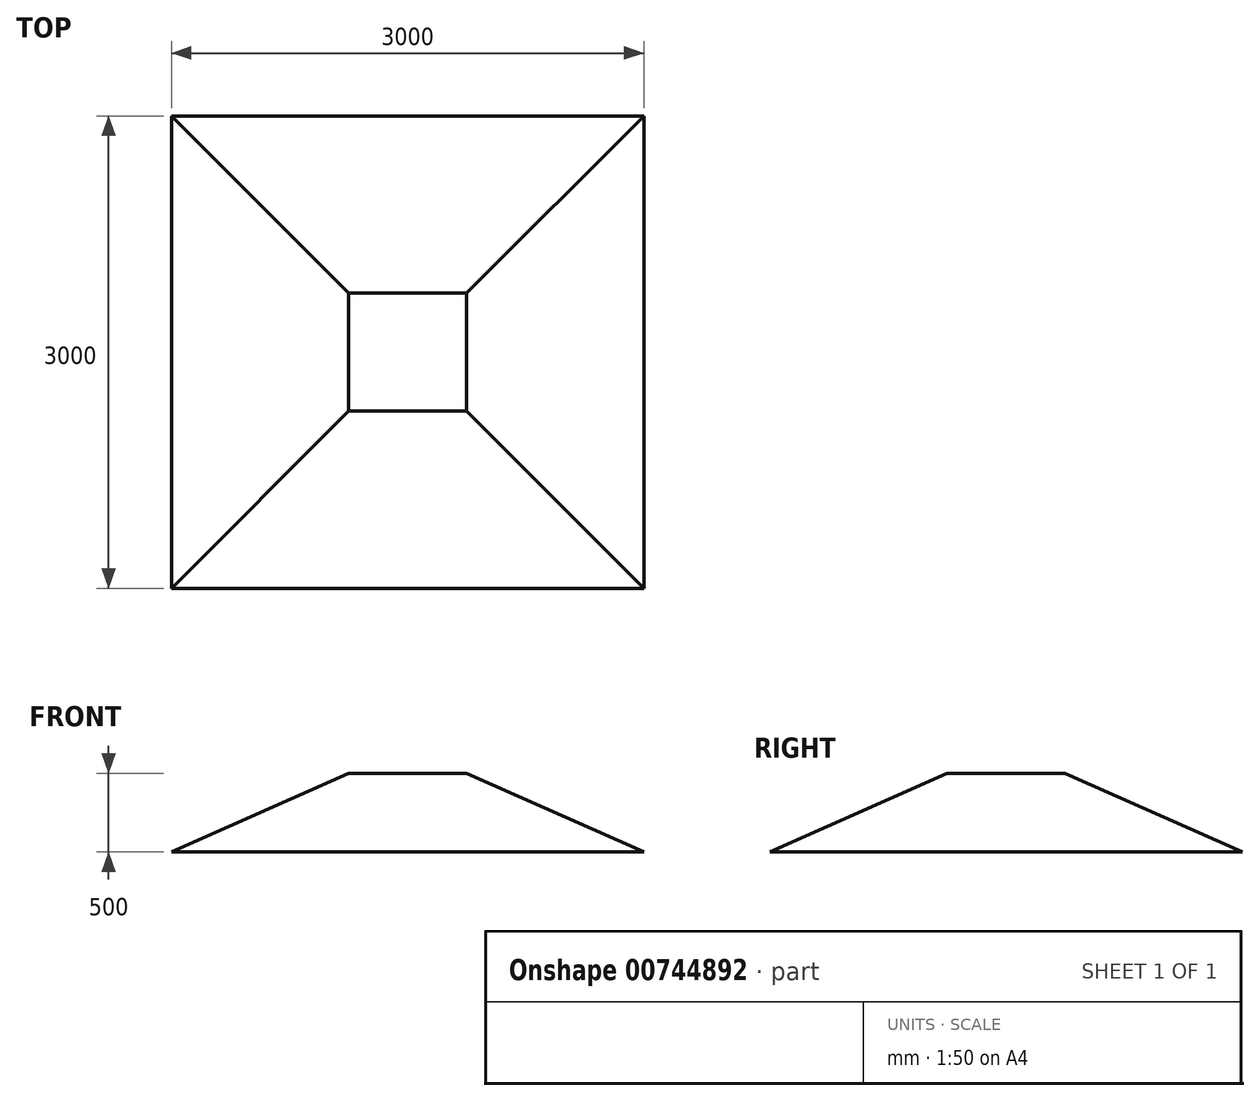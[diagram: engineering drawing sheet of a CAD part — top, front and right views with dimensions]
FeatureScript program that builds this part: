
annotation { "Feature Type Name" : "Feature", "Feature Type Description" : "" }
export const myFeature = defineFeature(function(context is Context, id is Id, definition is map)
    precondition{}
    {
        {
            var Q0;
            Q0=qCreatedBy(makeId("Top.planeOp"),FACE);
            var sketch = newSketch(context, id + "F0", { "sketchPlane" : qUnion([Q0])});
            skLineSegment(sketch, "E0.bottom", {"start": v(1500, 1500) * mm, "end": v(-1500, 1500) * mm});
            skLineSegment(sketch, "E0.top", {"start": v(1500, -1500) * mm, "end": v(-1500, -1500) * mm});
            skLineSegment(sketch, "E0.left", {"start": v(1500, 1500) * mm, "end": v(1500, -1500) * mm});
            skLineSegment(sketch, "E0.right", {"start": v(-1500, 1500) * mm, "end": v(-1500, -1500) * mm});
            skPoint(sketch, "E0.middle", {"position": v(0, 0) * mm});
            skSolve(sketch);
        }
        {
            var Q0;
            Q0=makeQuery(id+"F0.imprint","IMPRINT",FACE,{"disambiguationData":[TD([[makeQuery(id+"F0.imprint","IMPRINT",EDGE,{"derivedFrom":sQuery(id+"F0.wireOp",EDGE,"E0.bottom")}),1.0]])]});
            cPlane(context, id + "F1", {"entities" : qUnion([Q0]), "cplaneType" : CPlaneType.OFFSET, "offset" : 500 * mm, "width" : 150 * mm, "height" : 150 * mm});
        }
        {
            var Q0;
            Q0=qCreatedBy(id+"F1.planeOp",FACE);
            var sketch = newSketch(context, id + "F2", { "sketchPlane" : qUnion([Q0])});
            skLineSegment(sketch, "E1.bottom", {"start": v(375, 375) * mm, "end": v(-375, 375) * mm});
            skLineSegment(sketch, "E1.top", {"start": v(375, -375) * mm, "end": v(-375, -375) * mm});
            skLineSegment(sketch, "E1.left", {"start": v(375, 375) * mm, "end": v(375, -375) * mm});
            skLineSegment(sketch, "E1.right", {"start": v(-375, 375) * mm, "end": v(-375, -375) * mm});
            skPoint(sketch, "E1.middle", {"position": v(0, 0) * mm});
            skSolve(sketch);
        }
        {
            var Q0;
            Q0 = qSketchRegion(id + "F0", true);
            var Q1;
            Q1 = qSketchRegion(id + "F2", true);
            loft(context, id + "F3", {"sheetProfilesArray" : [{ "sheetProfileEntities" : qUnion([Q0]) }, { "sheetProfileEntities" : qUnion([Q1]) }]});
        }
    });
